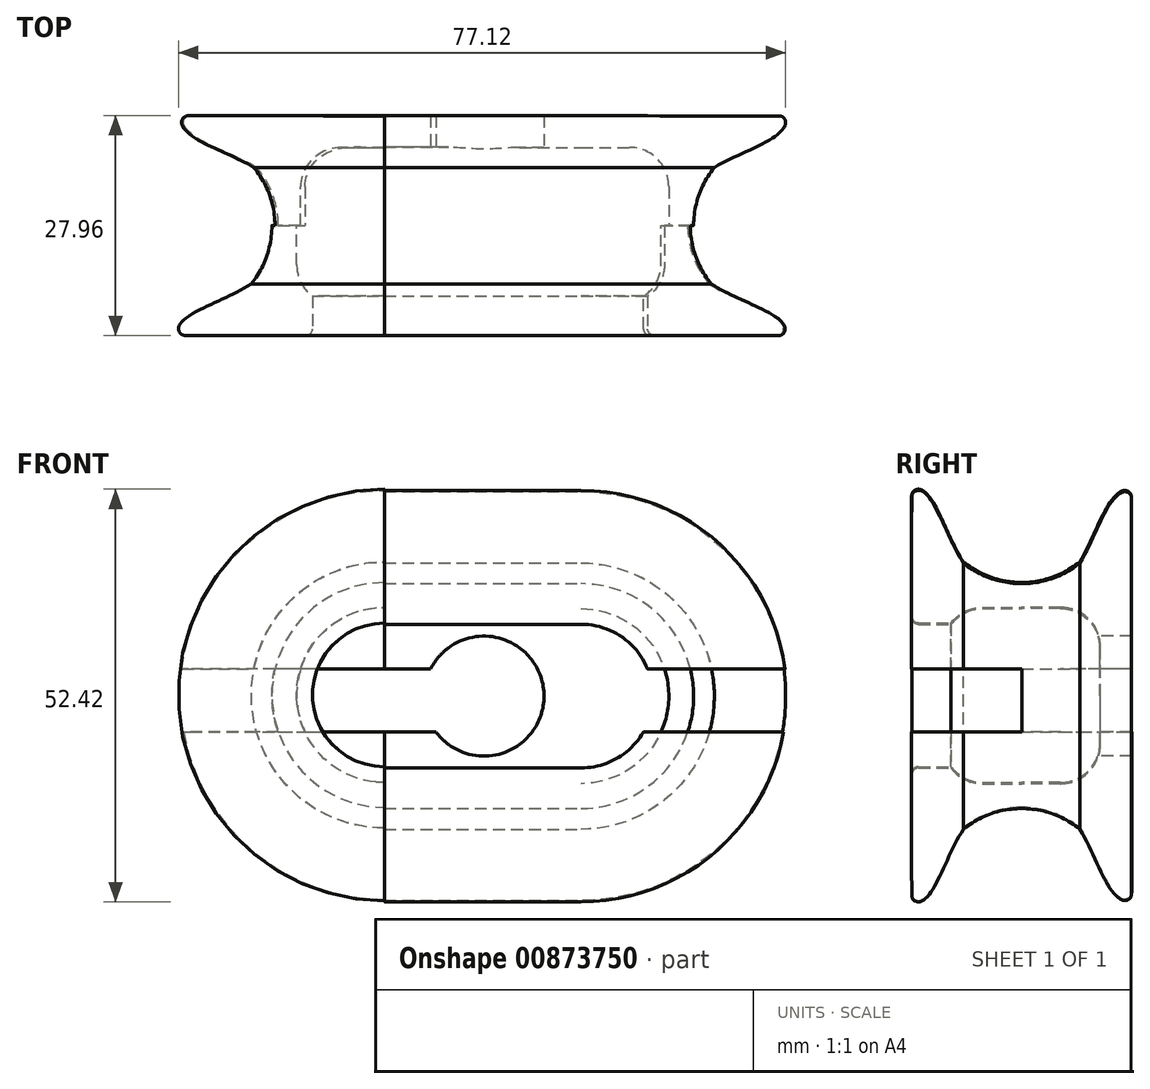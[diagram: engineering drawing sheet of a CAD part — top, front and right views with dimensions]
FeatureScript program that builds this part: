
annotation { "Feature Type Name" : "Feature", "Feature Type Description" : "" }
export const myFeature = defineFeature(function(context is Context, id is Id, definition is map)
    precondition{}
    {
        {
            var Q0;
            Q0=qCreatedBy(makeId("Top.planeOp"),FACE);
            var sketch = newSketch(context, id + "F0", { "sketchPlane" : qUnion([Q0])});
            skLineSegment(sketch, "E0", {"start": v(32.84, -14) * mm, "end": v(32.86, 13.93) * mm, "construction": true});
            skLineSegment(sketch, "E1", {"start": v(44, 13.93) * mm, "end": v(18.88, 13.93) * mm});
            skLineSegment(sketch, "E2", {"start": v(-31.68, 0) * mm, "end": v(56.18, -0.04) * mm, "construction": true});
            skLineSegment(sketch, "E3", {"start": v(26.86, 4.13) * mm, "end": v(26.83, 4.13) * mm, "construction": true});
            skFitSpline(sketch, "E4", {"points": [v(32.95, 4.2) * mm, v(44.88, 13.93) * mm], "startDerivative": vector(2.93, 13.74) * mm, "endDerivative": vector(-3.03, 11.76) * mm});
            skFitSpline(sketch, "E5.MirrorCS", {"points": [v(33.4, -4.44) * mm, v(44.71, -14) * mm], "startDerivative": vector(1.94, -13.96) * mm, "endDerivative": vector(-7.31, -9.9) * mm});
            skLineSegment(sketch, "E6", {"start": v(30.01, 4.92) * mm, "end": v(30.01, -0.03) * mm});
            skArc(sketch, "E7.filletArc", {"start": v(30.01, 4.92) * mm, "mid": v(28.55, 8.46) * mm, "end": v(25.01, 9.92) * mm});
            skArc(sketch, "E8.MirrorCS", {"start": v(30, -4.98) * mm, "mid": v(29.47, -7.22) * mm, "end": v(28, -8.99) * mm});
            skLineSegment(sketch, "E9.MirrorCS", {"start": v(30, -4.98) * mm, "end": v(30.01, -0.03) * mm});
            skLineSegment(sketch, "E10", {"start": v(28, -13.13) * mm, "end": v(28, -8.99) * mm});
            skLineSegment(sketch, "E11", {"start": v(4.88, 3.85) * mm, "end": v(44.88, 3.83) * mm, "construction": true});
            skLineSegment(sketch, "E12", {"start": v(44.88, 18.61) * mm, "end": v(44.88, -32.14) * mm, "construction": true});
            skLineSegment(sketch, "E13", {"start": v(25.01, 9.92) * mm, "end": v(18.88, 9.92) * mm});
            skLineSegment(sketch, "E14", {"start": v(44.15, -14) * mm, "end": v(28.85, -13.99) * mm});
            skLineSegment(sketch, "E15", {"start": v(36.5, -1.52) * mm, "end": v(36.51, 2.9) * mm, "construction": true});
            skArc(sketch, "E16", {"start": v(35.8, 7.37) * mm, "mid": v(33.16, -0.03) * mm, "end": v(35.8, -7.44) * mm});
            skArc(sketch, "E17.filletArc", {"start": v(44.15, -14) * mm, "mid": v(44.82, -13.68) * mm, "end": v(44.99, -12.96) * mm});
            skArc(sketch, "E18.filletArc", {"start": v(44.77, 12.71) * mm, "mid": v(44.72, 13.53) * mm, "end": v(44, 13.93) * mm});
            skPoint(sketch, "E19.visualSharp", {"position": v(28, -13.99) * mm});
            skArc(sketch, "E19.filletArc", {"start": v(28, -13.13) * mm, "mid": v(28.24, -13.74) * mm, "end": v(28.85, -13.99) * mm});
            skLineSegment(sketch, "E20", {"start": v(44, 13.93) * mm, "end": v(44.17, -17.26) * mm, "construction": true});
            skLineSegment(sketch, "E21", {"start": v(44.15, -14) * mm, "end": v(51.34, -14) * mm, "construction": true});
            skPoint(sketch, "E22", {"position": v(44.15, -14) * mm});
            skLineSegment(sketch, "E23", {"start": v(18.88, 13.93) * mm, "end": v(18.88, 9.92) * mm});
            skSolve(sketch);
        }
        {
            var Q0;
            Q0=makeQuery(id+"F0.imprint","IMPRINT",FACE,{"disambiguationData":[TD([[makeQuery(id+"F0.imprint","IMPRINT",EDGE,{"derivedFrom":sQuery(id+"F0.wireOp",EDGE,"E1")}),1.0]])]});
            var Q1;
            Q1=sQuery(id+"F0.wireOp",EDGE,"E23");
            revolve(context, id + "F1", {"surfaceOperationType" : NewSurfaceOperationType.NEW, "entities" : qUnion([Q0]), "axis" : qUnion([Q1]), "revolveType" : RevolveType.SYMMETRIC, "angle" : 180 * degree});
        }
        {
            var Q0;
            Q0=makeQuery(id+"F1.opRevolve","CAP_FACE",FACE,{"disambiguationData":[OSD([sQuery(id+"F0.wireOp",EDGE,"E1"),sQuery(id+"F0.wireOp",EDGE,"E4"),sQuery(id+"F0.wireOp",EDGE,"pFRlobtz-0q4r-BGyK-Zf5O-oVfqoQiTMujq"),sQuery(id+"F0.wireOp",EDGE,"0d47ac5b-4a7f-461a-a2c7-a7ca7c96fb220.MirrorCS"),sQuery(id+"F0.wireOp",EDGE,"E5.MirrorCS"),sQuery(id+"F0.wireOp",EDGE,"mUEO9S0t-vfNT-DUiq-7ehG-LlwwYBXUM1qr"),sQuery(id+"F0.wireOp",EDGE,"E6"),sQuery(id+"F0.wireOp",EDGE,"q7m8O1OS-iMQN-LF1h-SQSp-yMmx3rDaSw0e"),sQuery(id+"F0.wireOp",EDGE,"E7.filletArc"),sQuery(id+"F0.wireOp",EDGE,"E8.MirrorCS"),sQuery(id+"F0.wireOp",EDGE,"E9.MirrorCS"),sQuery(id+"F0.wireOp",EDGE,"DfFPZrzA-9eie-ccyR-lrFW-XJ07qiCjYuLb"),sQuery(id+"F0.wireOp",EDGE,"E10")])],"isStart":false});
            extrude(context, id + "F2", {"entities" : qUnion([Q0]), "operationType" : NewBodyOperationType.ADD, "depth" : 25 * mm, "offsetDistance" : 25 * mm});
        }
        {
            var Q0;
            Q0=makeQuery(id+"F2.opExtrude","CAP_FACE",FACE,{"disambiguationData":[OSD([sQuery(id+"F0.wireOp",EDGE,"E1"),sQuery(id+"F0.wireOp",EDGE,"E4"),sQuery(id+"F0.wireOp",EDGE,"pFRlobtz-0q4r-BGyK-Zf5O-oVfqoQiTMujq"),sQuery(id+"F0.wireOp",EDGE,"0d47ac5b-4a7f-461a-a2c7-a7ca7c96fb220.MirrorCS"),sQuery(id+"F0.wireOp",EDGE,"E5.MirrorCS"),sQuery(id+"F0.wireOp",EDGE,"mUEO9S0t-vfNT-DUiq-7ehG-LlwwYBXUM1qr"),sQuery(id+"F0.wireOp",EDGE,"E6"),sQuery(id+"F0.wireOp",EDGE,"q7m8O1OS-iMQN-LF1h-SQSp-yMmx3rDaSw0e"),sQuery(id+"F0.wireOp",EDGE,"E7.filletArc"),sQuery(id+"F0.wireOp",EDGE,"E8.MirrorCS"),sQuery(id+"F0.wireOp",EDGE,"E9.MirrorCS"),sQuery(id+"F0.wireOp",EDGE,"DfFPZrzA-9eie-ccyR-lrFW-XJ07qiCjYuLb"),sQuery(id+"F0.wireOp",EDGE,"E10")])],"isStart":false});
            cPlane(context, id + "F3", {"entities" : qUnion([Q0]), "cplaneType" : CPlaneType.OFFSET, "offset" : 0 * mm, "width" : 150 * mm, "height" : 150 * mm});
        }
        {
            var Q0;
            Q0=qCreatedBy(id+"F3.planeOp",FACE);
            var sketch = newSketch(context, id + "F4", { "sketchPlane" : qUnion([Q0])});
            skLineSegment(sketch, "E24", {"start": v(34.56, 15.08) * mm, "end": v(-53.3, 15.12) * mm, "construction": true});
            skLineSegment(sketch, "E25", {"start": v(-13.93, 25.28) * mm, "end": v(-13.93, 0.16) * mm});
            skLineSegment(sketch, "E26", {"start": v(0, -50.4) * mm, "end": v(0.04, 37.46) * mm, "construction": true});
            skLineSegment(sketch, "E27", {"start": v(-4.13, 8.14) * mm, "end": v(-4.13, 8.1) * mm, "construction": true});
            skFitSpline(sketch, "E28", {"points": [v(-4.2, 14.23) * mm, v(-13.93, 26.16) * mm], "startDerivative": vector(-13.74, 2.93) * mm, "endDerivative": vector(-11.76, -3.03) * mm});
            skFitSpline(sketch, "E29.MirrorCS", {"points": [v(4.44, 14.68) * mm, v(14, 25.99) * mm], "startDerivative": vector(13.96, 1.94) * mm, "endDerivative": vector(9.9, -7.31) * mm});
            skLineSegment(sketch, "E30", {"start": v(-4.92, 11.29) * mm, "end": v(0.03, 11.29) * mm});
            skArc(sketch, "E31.filletArc", {"start": v(-4.92, 11.29) * mm, "mid": v(-8.46, 9.82) * mm, "end": v(-9.92, 6.29) * mm});
            skArc(sketch, "E32.MirrorCS", {"start": v(4.98, 11.28) * mm, "mid": v(7.22, 10.75) * mm, "end": v(8.99, 9.27) * mm});
            skLineSegment(sketch, "E33.MirrorCS", {"start": v(4.98, 11.28) * mm, "end": v(0.03, 11.29) * mm});
            skLineSegment(sketch, "E34", {"start": v(13.13, 9.27) * mm, "end": v(8.99, 9.27) * mm});
            skLineSegment(sketch, "E35", {"start": v(-9.92, 6.29) * mm, "end": v(-9.92, 0.16) * mm});
            skLineSegment(sketch, "E36", {"start": v(14, 25.43) * mm, "end": v(13.99, 10.12) * mm});
            skArc(sketch, "E37", {"start": v(-7.37, 17.07) * mm, "mid": v(0.03, 14.43) * mm, "end": v(7.44, 17.07) * mm});
            skArc(sketch, "E38.filletArc", {"start": v(14, 25.43) * mm, "mid": v(13.68, 26.1) * mm, "end": v(12.96, 26.26) * mm});
            skArc(sketch, "E39.filletArc", {"start": v(-12.71, 26.05) * mm, "mid": v(-13.53, 26) * mm, "end": v(-13.93, 25.28) * mm});
            skPoint(sketch, "E40.visualSharp", {"position": v(13.99, 9.27) * mm});
            skArc(sketch, "E40.filletArc", {"start": v(13.13, 9.27) * mm, "mid": v(13.74, 9.52) * mm, "end": v(13.99, 10.12) * mm});
            skLineSegment(sketch, "E41", {"start": v(14, 25.43) * mm, "end": v(14, 32.62) * mm, "construction": true});
            skPoint(sketch, "E42", {"position": v(14, 25.43) * mm});
            skLineSegment(sketch, "E43", {"start": v(-13.93, 0.16) * mm, "end": v(-9.92, 0.16) * mm});
            skPoint(sketch, "E44", {"position": v(-13.93, -18.72) * mm});
            skSolve(sketch);
        }
        {
            var Q0;
            Q0=makeQuery(id+"F4.imprint","IMPRINT",FACE,{"disambiguationData":[TD([[makeQuery(id+"F4.imprint","IMPRINT",EDGE,{"derivedFrom":sQuery(id+"F4.wireOp",EDGE,"E25")}),1.0]])]});
            var Q1;
            Q1=sQuery(id+"F4.wireOp",EDGE,"E43");
            revolve(context, id + "F5", {"operationType" : NewBodyOperationType.ADD, "surfaceOperationType" : NewSurfaceOperationType.NEW, "entities" : qUnion([Q0]), "axis" : qUnion([Q1]), "revolveType" : RevolveType.ONE_DIRECTION, "angle" : 180 * degree});
        }
        {
            var Q0;
            Q0=qCreatedBy(makeId("Front.planeOp"),FACE);
            var sketch = newSketch(context, id + "F6", { "sketchPlane" : qUnion([Q0])});
            skLineSegment(sketch, "E45", {"start": v(29.26, 0) * mm, "end": v(-58.04, 0) * mm, "construction": true});
            skLineSegment(sketch, "E46", {"start": v(6.54, -28.68) * mm, "end": v(6.54, 40.74) * mm, "construction": true});
            skLineSegment(sketch, "E47.bottom", {"start": v(-0.27, 3.43) * mm, "end": v(-28.46, 3.43) * mm});
            skLineSegment(sketch, "E47.top", {"start": v(0.44, -4.57) * mm, "end": v(-28.46, -4.57) * mm});
            skPoint(sketch, "E48", {"position": v(6.54, 0) * mm});
            skArc(sketch, "E49", {"start": v(-0.27, 3.43) * mm, "mid": v(14.13, 0.67) * mm, "end": v(0.44, -4.57) * mm});
            skLineSegment(sketch, "E50", {"start": v(-53.84, 3.43) * mm, "end": v(-53.84, -4.57) * mm});
            skLineSegment(sketch, "E51", {"start": v(-53.84, -4.57) * mm, "end": v(-28.46, -4.57) * mm});
            skLineSegment(sketch, "E52", {"start": v(-28.46, 3.43) * mm, "end": v(-53.84, 3.43) * mm});
            skLineSegment(sketch, "E53", {"start": v(8.18, 3.43) * mm, "end": v(8.18, -4.57) * mm, "construction": true});
            skLineSegment(sketch, "E54", {"start": v(64.91, 3.43) * mm, "end": v(13.34, 3.43) * mm});
            skLineSegment(sketch, "E55", {"start": v(12.64, -4.57) * mm, "end": v(64.91, -4.57) * mm});
            skLineSegment(sketch, "E56", {"start": v(64.91, 3.43) * mm, "end": v(64.91, -4.57) * mm});
            skSolve(sketch);
        }
        {
            var Q0;
            Q0=makeQuery(id+"F6.imprint","IMPRINT",FACE,{"disambiguationData":[TD([[makeQuery(id+"F6.imprint","IMPRINT",EDGE,{"derivedFrom":sQuery(id+"F6.wireOp",EDGE,"E47.bottom")}),1.0]])]});
            extrude(context, id + "F7", {"entities" : qUnion([Q0]), "operationType" : NewBodyOperationType.REMOVE, "oppositeDirection" : true, "depth" : 15 * mm, "offsetDistance" : 25 * mm});
        }
        {
            var Q0;
            {var subQ0=sQuery(id+"F6.wireOp",EDGE,"E54");Q0=makeQuery(id+"F6.imprint","IMPRINT",FACE,{"disambiguationData":[TD([[makeQuery(id+"F6.imprint","IMPRINT",EDGE,{"derivedFrom":subQ0}),1.0]])]});}
            extrude(context, id + "F8", {"entities" : qUnion([Q0]), "operationType" : NewBodyOperationType.REMOVE, "depth" : 20 * mm, "offsetDistance" : 25 * mm});
        }
    });
